# Revit family: Haworth_HC1Pedestal_9HE_EU_PRELIMINARY
name_source: partatom
category: Furniture Systems
units: mm (PartAtom-declared; Revit-internal decimal feet)

## family parameters
Always vertical = Yes
Cut with Voids When Loaded = No
OmniClass Number = 23.40.70.14.64.21
OmniClass Title = Systems Furniture
Part Type = Normal
Room Calculation Point = No
Round Connector Dimension = Use Diameter
Shared = No
Work Plane-Based = No

## types (4) — shared parameters
70D Top = No
Actual Height = 52 cm
Actual Width = 43 cm
Assembly Code = E2020200
Depth of Top = if(Depth 60, 60, 70), if(Depth 80, 80, 90)
Description = Haworth - HC1 Pedestal - 9HE Pedestal
Four Doors Recessed Handle Door = No
Glide Finish = Haworth _ Polymer _ Black
Handle 128 128 = No
Handle 2 = No
Manufacturer = Haworth
Model = MS900XXXXX
Pull Finish = Haworth _ Paint _ Smooth Plaster
Recessed Handle 128 = No
Recessed Handle 128 1H Upper = No
Revision Number = 1
Size = Verify Final Dim. w/ Haworth
Standard Handle 2 = No
URL = https://www.haworth.com
URL - Product = https://www.haworth.com
Warranty = http://www.haworth.com
Without Pull = No

## per-type parameters (varying)
| type | 1H Upper | 2H Middle | 3H Lower | 3H Middle | 3H Upper | 60D Top | 6H Lower | 80D Top | 90D Top | Actual Depth | Casters | Four Doors | Glides | Handle 1 | Handle Metal | High | Large | Low | Small | Standard Handle 1 | Thickness | Top Depth |
| 3/3/3 43.3 x 80 x 51.6 | No | No | Yes | Yes | Yes | No | No | No | Yes | 80 cm | No | No | Yes | No | No | Yes | Yes | No | No | Yes | 3 cm | 90 cm |
| 1/2/3/3 43.3 x 80 x 51.6 | Yes | Yes | Yes | Yes | No | No | No | No | Yes | 80 cm | Yes | Yes | No | No | Yes | No | Yes | Yes | No | No | 2 cm | 90 cm |
| 1/2/6 43.3 x 80 x 51.6 | Yes | Yes | No | No | No | No | Yes | Yes | No | 80 cm | Yes | No | No | Yes | No | No | Yes | Yes | No | No | 2 cm | 80 cm |
| 1/2/3/3 43.3 x 60 x 51.6 | Yes | Yes | Yes | Yes | No | Yes | No | No | No | 60 cm | Yes | Yes | No | Yes | No | No | No | Yes | Yes | No | 2 cm | 60 cm |

## geometry (parser evidence)
native form markers: Sweep x15
no freeform markers — native parametric forms only
